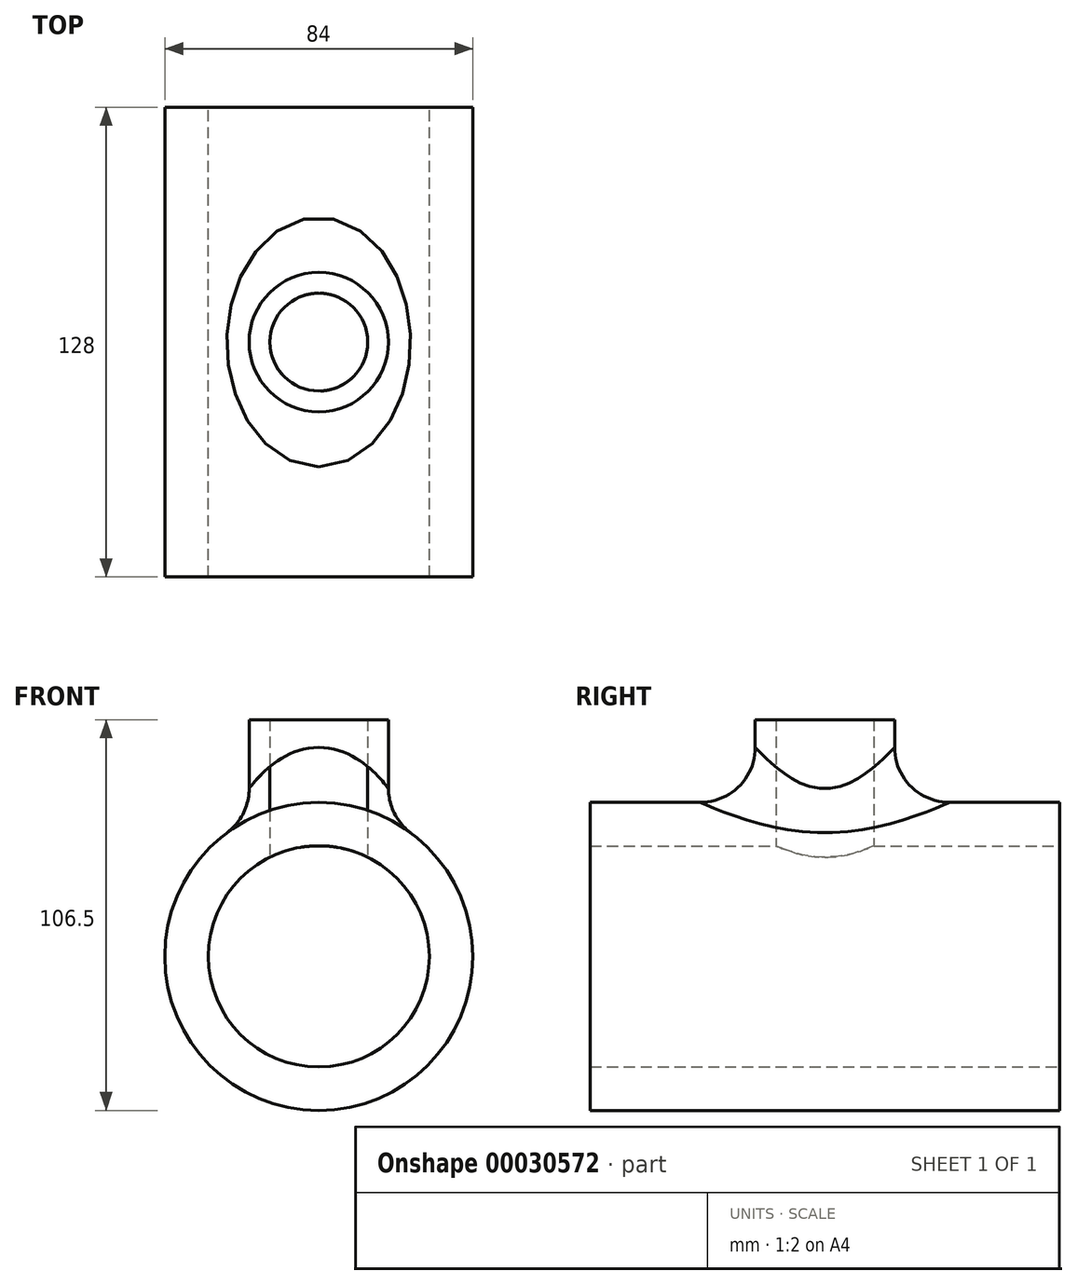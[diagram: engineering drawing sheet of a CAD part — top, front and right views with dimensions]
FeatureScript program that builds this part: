
annotation { "Feature Type Name" : "Feature", "Feature Type Description" : "" }
export const myFeature = defineFeature(function(context is Context, id is Id, definition is map)
    precondition{}
    {
        {
            var Q0;
            Q0=qCreatedBy(makeId("Front.planeOp"),FACE);
            var sketch = newSketch(context, id + "F0", { "sketchPlane" : qUnion([Q0])});
            skCircle(sketch, "E0", {"center": v(0, -42) * mm, "radius": 42 * mm});
            skCircle(sketch, "E1", {"center": v(0, -42) * mm, "radius": 30.15 * mm});
            skSolve(sketch);
        }
        {
            var Q0;
            Q0 = qSketchRegion(id + "F0", true);
            extrude(context, id + "F1", {"entities" : qUnion([Q0]), "endBound" : BoundingType.SYMMETRIC, "depth" : 128 * mm});
        }
        {
            var Q0;
            Q0=qCreatedBy(makeId("Top.planeOp"),FACE);
            var sketch = newSketch(context, id + "F2", { "sketchPlane" : qUnion([Q0])});
            skCircle(sketch, "E2", {"center": v(0, 0) * mm, "radius": 19 * mm});
            skCircle(sketch, "E3", {"center": v(0, 0) * mm, "radius": 13.34 * mm});
            skSolve(sketch);
        }
        {
            var Q0;
            Q0=makeQuery(id+"F2.imprint","IMPRINT",FACE,{"disambiguationData":[TD([[makeQuery(id+"F2.imprint","IMPRINT",EDGE,{"derivedFrom":sQuery(id+"F2.wireOp",EDGE,"E2")}),1.0]])]});
            var Q1;
            Q1=makeQuery(id+"F1.opExtrude","SWEPT_FACE",FACE,{"disambiguationData":[OSD([sQuery(id+"F0.wireOp",EDGE,"E1")])]});
            extrude(context, id + "F3", {"entities" : qUnion([Q0]), "operationType" : NewBodyOperationType.ADD, "depth" : 22.5 * mm, "hasSecondDirection" : true, "secondDirectionBound" : SecondDirectionBoundingType.UP_TO_SURFACE, "secondDirectionOppositeDirection" : true, "secondDirectionBoundEntityFace" : qUnion([Q1]), "secondDirectionDepth" : 25 * mm});
        }
        {
            var Q0;
            Q0=makeQuery(id+"F3.opExtrude","CAP_FACE",FACE,{"disambiguationData":[OSD([sQuery(id+"F2.wireOp",EDGE,"E2"),sQuery(id+"F2.wireOp",EDGE,"E3")]),OD(1.0)],"isStart":false});
            var sketch = newSketch(context, id + "F4", { "sketchPlane" : qUnion([Q0])});
            skCircle(sketch, "E4.0", {"center": v(0, 0) * mm, "radius": 13.34 * mm});
            skSolve(sketch);
        }
        {
            var Q0;
            Q0 = qSketchRegion(id + "F4", true);
            var Q1;
            Q1=makeQuery(id+"F1.opExtrude","SWEPT_FACE",FACE,{"disambiguationData":[OSD([sQuery(id+"F0.wireOp",EDGE,"E1")])]});
            extrude(context, id + "F5", {"entities" : qUnion([Q0]), "operationType" : NewBodyOperationType.REMOVE, "endBound" : BoundingType.UP_TO_SURFACE, "oppositeDirection" : true, "endBoundEntityFace" : qUnion([Q1]), "depth" : 25 * mm});
        }
        {
            var Q0;
            Q0=makeQuery(id+"F3.boolean.opBoolean","INTERSECT",EDGE,{"derivedFrom":[makeQuery(id+"F1.opExtrude","SWEPT_FACE",FACE,{"disambiguationData":[OSD([sQuery(id+"F0.wireOp",EDGE,"E0")])]}),makeQuery(id+"F3.opExtrude","SWEPT_FACE",FACE,{"disambiguationData":[OSD([sQuery(id+"F2.wireOp",EDGE,"E2")])]})]});
            fillet(context, id + "F6", {"entities" : qUnion([Q0]), "radius" : 15 * mm, "tangentPropagation" : true, "allowEdgeOverflow" : false});
        }
    });
